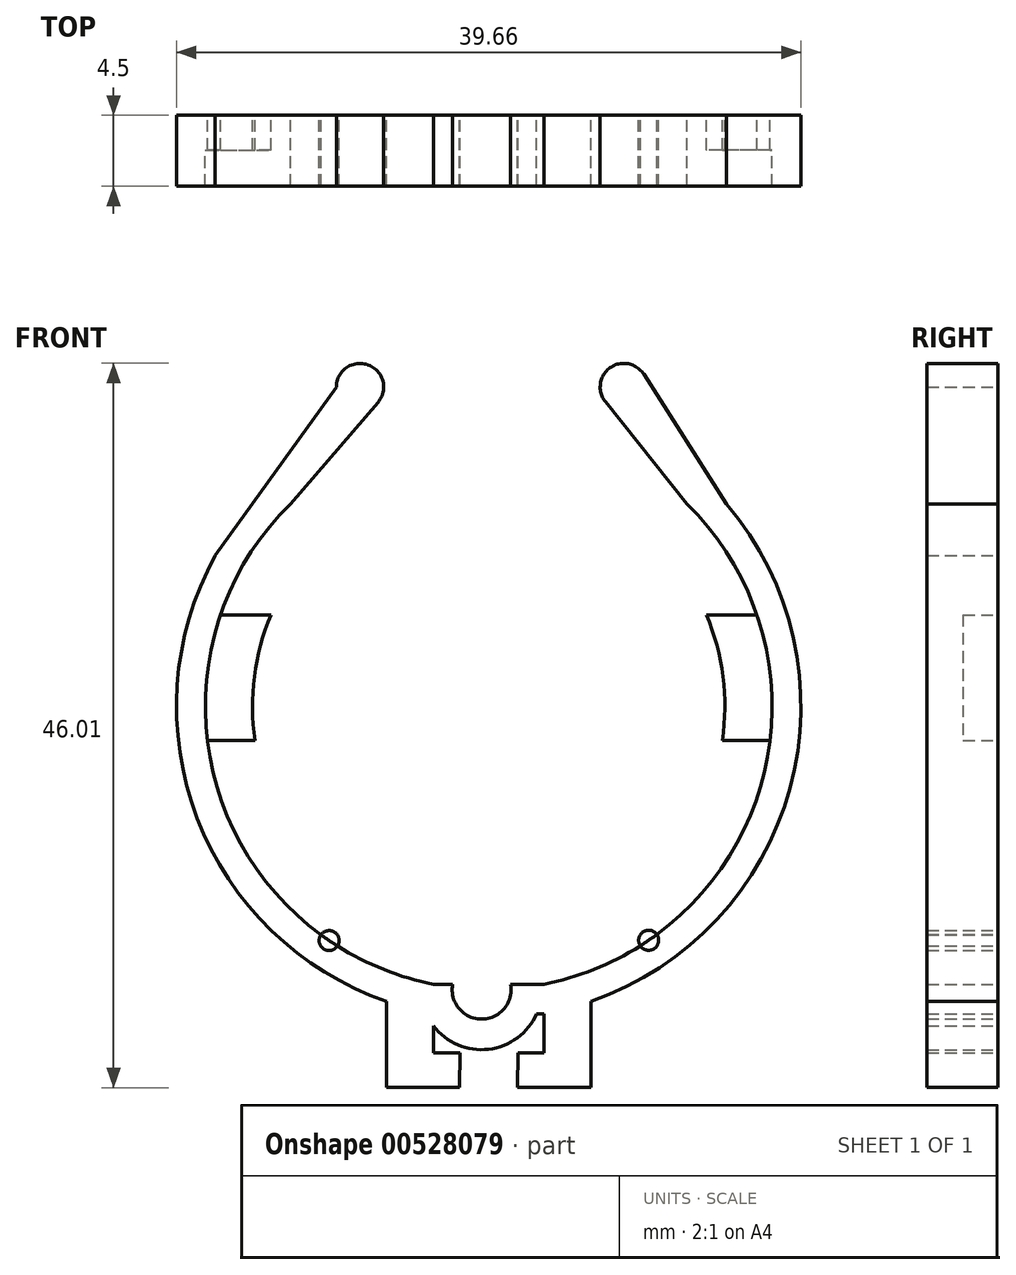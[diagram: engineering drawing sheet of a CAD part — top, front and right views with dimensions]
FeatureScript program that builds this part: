
annotation { "Feature Type Name" : "Feature", "Feature Type Description" : "" }
export const myFeature = defineFeature(function(context is Context, id is Id, definition is map)
    precondition{}
    {
        {
            var Q0;
            Q0=qCreatedBy(makeId("Front.planeOp"),FACE);
            var sketch = newSketch(context, id + "F0", { "sketchPlane" : qUnion([Q0])});
            skArc(sketch, "E0", {"start": v(-17.37, 9.57) * mm, "mid": v(-17.9, -8.53) * mm, "end": v(-3.5, -19.52) * mm});
            skArc(sketch, "E1", {"start": v(-12.6, 12.86) * mm, "mid": v(-17.25, -5.14) * mm, "end": v(-3.5, -17.66) * mm});
            skArc(sketch, "E2", {"start": v(-13.83, 5.82) * mm, "mid": v(-14.88, 1.89) * mm, "end": v(-14.84, -2.18) * mm});
            skLineSegment(sketch, "E3", {"start": v(-17.03, 5.82) * mm, "end": v(-13.83, 5.82) * mm});
            skLineSegment(sketch, "E4", {"start": v(-17.87, -2.18) * mm, "end": v(-14.84, -2.18) * mm});
            skLineSegment(sketch, "E5", {"start": v(17.87, -2.18) * mm, "end": v(14.84, -2.18) * mm});
            skLineSegment(sketch, "E6", {"start": v(17.03, 5.82) * mm, "end": v(13.83, 5.82) * mm});
            skArc(sketch, "E7.trimOffspring", {"start": v(14.84, -2.18) * mm, "mid": v(14.88, 1.89) * mm, "end": v(13.83, 5.82) * mm});
            skLineSegment(sketch, "E8", {"start": v(-12.6, 12.86) * mm, "end": v(-17.37, 9.57) * mm});
            skLineSegment(sketch, "E9", {"start": v(12.6, 12.86) * mm, "end": v(15.1, 12.86) * mm});
            skLineSegment(sketch, "E10.top", {"start": v(-6.5, -24.22) * mm, "end": v(-1.85, -24.22) * mm});
            skLineSegment(sketch, "E10.left", {"start": v(-6.5, -18.73) * mm, "end": v(-6.5, -24.22) * mm});
            skLineSegment(sketch, "E10.right", {"start": v(6.5, -18.73) * mm, "end": v(6.5, -24.22) * mm});
            skCircle(sketch, "E11", {"center": v(-8.17, 20.29) * mm, "radius": 1.5 * mm});
            skCircle(sketch, "E12", {"center": v(8.58, 20.29) * mm, "radius": 1.5 * mm});
            skLineSegment(sketch, "E13", {"start": v(-9.67, 20.29) * mm, "end": v(-17.37, 9.57) * mm});
            skLineSegment(sketch, "E14", {"start": v(-12.6, 12.86) * mm, "end": v(-7.04, 19.3) * mm});
            skLineSegment(sketch, "E15", {"start": v(12.6, 12.86) * mm, "end": v(7.4, 19.35) * mm});
            skLineSegment(sketch, "E16", {"start": v(15.1, 12.86) * mm, "end": v(9.85, 21.1) * mm});
            skCircle(sketch, "E17", {"center": v(10.16, -14.86) * mm, "radius": 0.64 * mm});
            skCircle(sketch, "E18", {"center": v(-10.13, -14.88) * mm, "radius": 0.64 * mm});
            skLineSegment(sketch, "E19.left", {"start": v(-1.85, -24.22) * mm, "end": v(-1.83, -22) * mm});
            skLineSegment(sketch, "E19.right", {"start": v(1.83, -24.22) * mm, "end": v(1.85, -22) * mm});
            skPoint(sketch, "E19.middle", {"position": v(0, -23.1) * mm});
            skLineSegment(sketch, "E20.trimOffspring", {"start": v(1.83, -24.22) * mm, "end": v(6.5, -24.22) * mm});
            skLineSegment(sketch, "E21.top", {"start": v(-3.5, -22) * mm, "end": v(-1.83, -22) * mm});
            skLineSegment(sketch, "E21.left", {"start": v(-3.5, -17.66) * mm, "end": v(-3.5, -22) * mm});
            skLineSegment(sketch, "E21.right", {"start": v(3.5, -17.66) * mm, "end": v(3.5, -22) * mm});
            skPoint(sketch, "E21.middle", {"position": v(0, -19.83) * mm});
            skArc(sketch, "E22.trimOffspring", {"start": v(3.5, -17.66) * mm, "mid": v(17.25, -5.14) * mm, "end": v(12.6, 12.86) * mm});
            skArc(sketch, "E23.trimOffspring", {"start": v(3.5, -19.52) * mm, "mid": v(18.67, -6.69) * mm, "end": v(15.1, 12.86) * mm});
            skArc(sketch, "E24", {"start": v(-3.95, -19.52) * mm, "mid": v(-0.45, -21.8) * mm, "end": v(3.05, -19.52) * mm});
            skLineSegment(sketch, "E25", {"start": v(-4.25, -17.66) * mm, "end": v(-3.5, -17.66) * mm});
            skLineSegment(sketch, "E26", {"start": v(3.5, -17.66) * mm, "end": v(3.35, -17.66) * mm});
            skLineSegment(sketch, "E27", {"start": v(-3.95, -19.52) * mm, "end": v(-3.5, -19.52) * mm});
            skLineSegment(sketch, "E28", {"start": v(3.5, -19.52) * mm, "end": v(3.05, -19.52) * mm});
            skLineSegment(sketch, "E29.trimOffspring", {"start": v(1.85, -22) * mm, "end": v(3.5, -22) * mm});
            skLineSegment(sketch, "E30", {"start": v(-4.25, -17.66) * mm, "end": v(-2.85, -17.66) * mm});
            skLineSegment(sketch, "E31", {"start": v(3.35, -17.66) * mm, "end": v(2.32, -17.66) * mm});
            skArc(sketch, "E32", {"start": v(-2.29, -17.66) * mm, "mid": v(-0.45, -19.87) * mm, "end": v(1.4, -17.66) * mm});
            skLineSegment(sketch, "E33", {"start": v(-2.85, -17.66) * mm, "end": v(-2.29, -17.66) * mm});
            skLineSegment(sketch, "E34", {"start": v(2.32, -17.66) * mm, "end": v(1.4, -17.66) * mm});
            skSolve(sketch);
        }
        {
            var Q0;
            Q0=makeQuery(id+"F0.imprint","IMPRINT",FACE,{"disambiguationData":[TD([[makeQuery(id+"F0.imprint","IMPRINT",EDGE,{"derivedFrom":sQuery(id+"F0.wireOp",EDGE,"E0")}),1.0]])]});
            var Q1;
            Q1=makeQuery(id+"F0.imprint","IMPRINT",FACE,{"disambiguationData":[TD([[makeQuery(id+"F0.imprint","IMPRINT",EDGE,{"derivedFrom":sQuery(id+"F0.wireOp",EDGE,"E24")}),1.0]])]});
            var Q2;
            Q2=makeQuery(id+"F0.imprint","IMPRINT",FACE,{"disambiguationData":[TD([[makeQuery(id+"F0.imprint","IMPRINT",EDGE,{"derivedFrom":sQuery(id+"F0.wireOp",EDGE,"E10.top")}),1.0]])]});
            var Q3;
            {var subQ4=sQuery(id+"F0.wireOp",EDGE,"E10.right");Q3=makeQuery(id+"F0.imprint","IMPRINT",FACE,{"disambiguationData":[TD([[makeQuery(id+"F0.imprint","IMPRINT",EDGE,{"derivedFrom":subQ4}),-1.0]])]});}
            var Q4;
            {var subQ8=sQuery(id+"F0.wireOp",EDGE,"E9");Q4=makeQuery(id+"F0.imprint","IMPRINT",FACE,{"disambiguationData":[TD([[makeQuery(id+"F0.imprint","IMPRINT",EDGE,{"derivedFrom":subQ8}),-1.0]])]});}
            var Q5;
            Q5=makeQuery(id+"F0.imprint","IMPRINT",FACE,{"disambiguationData":[TD([[makeQuery(id+"F0.imprint","IMPRINT",EDGE,{"derivedFrom":sQuery(id+"F0.wireOp",EDGE,"E9")}),1.0]])]});
            var Q6;
            {var subQ0=sQuery(id+"F0.wireOp",EDGE,"E12");var subQ1=makeQuery(id+"F0.imprint","INTERSECT",VERTEX,{"derivedFrom":[subQ0,sQuery(id+"F0.wireOp",EDGE,"E15")]});Q6=makeQuery(id+"F0.imprint","IMPRINT",FACE,{"disambiguationData":[TD([[makeQuery(id+"F0.imprint","IMPRINT",EDGE,{"disambiguationData":[TD([[subQ1,1.0]])],"derivedFrom":subQ0}),1.0]])]});}
            var Q7;
            {var subQ0=sQuery(id+"F0.wireOp",EDGE,"E11");var subQ1=makeQuery(id+"F0.imprint","INTERSECT",VERTEX,{"derivedFrom":[subQ0,sQuery(id+"F0.wireOp",EDGE,"E13")]});Q7=makeQuery(id+"F0.imprint","IMPRINT",FACE,{"disambiguationData":[TD([[makeQuery(id+"F0.imprint","IMPRINT",EDGE,{"disambiguationData":[TD([[subQ1,-1.0]])],"derivedFrom":subQ0}),1.0]])]});}
            var Q8;
            Q8=makeQuery(id+"F0.imprint","IMPRINT",FACE,{"disambiguationData":[TD([[makeQuery(id+"F0.imprint","IMPRINT",EDGE,{"derivedFrom":sQuery(id+"F0.wireOp",EDGE,"E8")}),-1.0]])]});
            var Q9;
            {var subQ0=sQuery(id+"F0.wireOp",EDGE,"E18");var subQ1=sQuery(id+"F0.wireOp",EDGE,"E1");var subQ2=makeQuery(id+"F0.imprint","INTERSECT",VERTEX,{"disambiguationData":[OD(0.0)],"derivedFrom":[subQ1,subQ0]});Q9=makeQuery(id+"F0.imprint","IMPRINT",FACE,{"disambiguationData":[TD([[makeQuery(id+"F0.imprint","IMPRINT",EDGE,{"disambiguationData":[TD([[subQ2,-1.0]])],"derivedFrom":subQ1}),1.0]])]});}
            var Q10;
            {var subQ0=sQuery(id+"F0.wireOp",EDGE,"E22.trimOffspring");var subQ1=sQuery(id+"F0.wireOp",EDGE,"E17");var subQ2=makeQuery(id+"F0.imprint","INTERSECT",VERTEX,{"disambiguationData":[OD(0.0)],"derivedFrom":[subQ1,subQ0]});Q10=makeQuery(id+"F0.imprint","IMPRINT",FACE,{"disambiguationData":[TD([[makeQuery(id+"F0.imprint","IMPRINT",EDGE,{"disambiguationData":[TD([[subQ2,1.0]])],"derivedFrom":subQ1}),1.0]])]});}
            var Q11;
            {var subQ8=sQuery(id+"F0.wireOp",EDGE,"E26");Q11=makeQuery(id+"F0.imprint","IMPRINT",FACE,{"disambiguationData":[TD([[makeQuery(id+"F0.imprint","IMPRINT",EDGE,{"derivedFrom":subQ8}),1.0]])]});}
            extrude(context, id + "F1", {"entities" : qUnion([Q0, Q1, Q2, Q3, Q4, Q5, Q6, Q7, Q8, Q9, Q10, Q11]), "depth" : 4.5 * mm, "offsetDistance" : 25.4 * mm});
        }
        {
            var Q0;
            Q0=makeQuery(id+"F0.imprint","IMPRINT",FACE,{"disambiguationData":[TD([[makeQuery(id+"F0.imprint","IMPRINT",EDGE,{"derivedFrom":sQuery(id+"F0.wireOp",EDGE,"E2")}),-1.0]])]});
            var Q1;
            {var subQ0=sQuery(id+"F0.wireOp",EDGE,"E5");Q1=makeQuery(id+"F0.imprint","IMPRINT",FACE,{"disambiguationData":[TD([[makeQuery(id+"F0.imprint","IMPRINT",EDGE,{"derivedFrom":subQ0}),-1.0]])]});}
            extrude(context, id + "F2", {"entities" : qUnion([Q0, Q1]), "operationType" : NewBodyOperationType.ADD, "depth" : 2.2 * mm, "offsetDistance" : 25.4 * mm});
        }
    });
